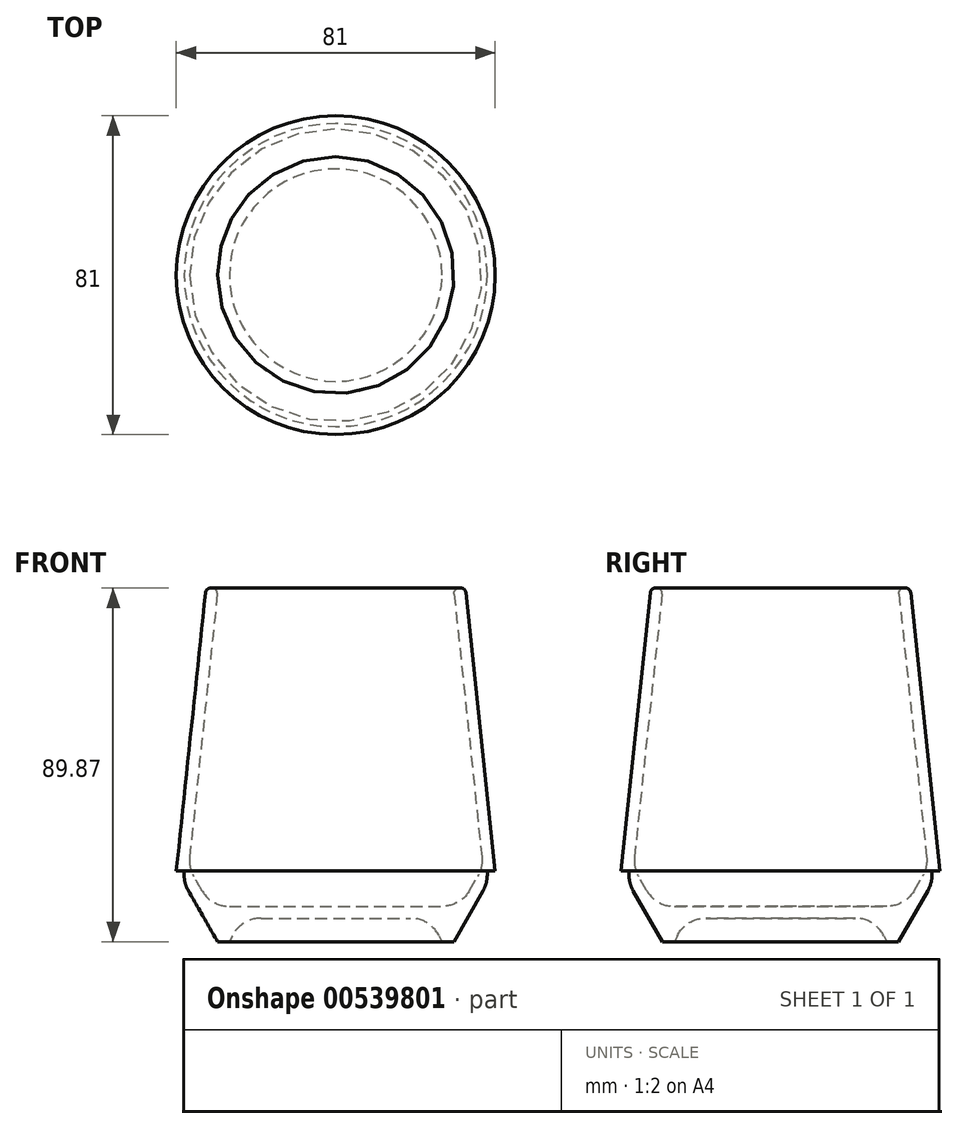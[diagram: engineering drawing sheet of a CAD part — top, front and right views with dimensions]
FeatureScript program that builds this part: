
annotation { "Feature Type Name" : "Feature", "Feature Type Description" : "" }
export const myFeature = defineFeature(function(context is Context, id is Id, definition is map)
    precondition{}
    {
        {
            var Q0;
            Q0=qCreatedBy(makeId("Front.planeOp"),FACE);
            var sketch = newSketch(context, id + "F0", { "sketchPlane" : qUnion([Q0])});
            skLineSegment(sketch, "E0", {"start": v(0, 6) * mm, "end": v(19, 6) * mm});
            skLineSegment(sketch, "E1", {"start": v(26.24, 1.52) * mm, "end": v(27, 0) * mm});
            skLineSegment(sketch, "E2", {"start": v(27, 0) * mm, "end": v(30, 0) * mm});
            skLineSegment(sketch, "E3", {"start": v(30, 0) * mm, "end": v(37.43, 12.97) * mm});
            skLineSegment(sketch, "E4", {"start": v(38.5, 17) * mm, "end": v(38.5, 18) * mm});
            skLineSegment(sketch, "E5", {"start": v(38.5, 18) * mm, "end": v(40.5, 18) * mm});
            skLineSegment(sketch, "E6", {"start": v(40.5, 18) * mm, "end": v(33.07, 88.7) * mm});
            skLineSegment(sketch, "E7", {"start": v(31.64, 89.86) * mm, "end": v(31.24, 89.82) * mm});
            skLineSegment(sketch, "E8", {"start": v(30.08, 88.4) * mm, "end": v(37.11, 21.54) * mm});
            skLineSegment(sketch, "E9", {"start": v(36.09, 16.67) * mm, "end": v(34.03, 13.08) * mm});
            skLineSegment(sketch, "E10", {"start": v(27, 9) * mm, "end": v(0, 9) * mm});
            skLineSegment(sketch, "E11", {"start": v(0, 9) * mm, "end": v(0, 6) * mm});
            skPoint(sketch, "E12.visualSharp", {"position": v(24, 6) * mm});
            skArc(sketch, "E12.filletArc", {"start": v(26.24, 1.52) * mm, "mid": v(23.25, 4.8) * mm, "end": v(19, 6) * mm});
            skPoint(sketch, "E13.visualSharp", {"position": v(31.7, 9) * mm});
            skArc(sketch, "E13.filletArc", {"start": v(27, 9) * mm, "mid": v(31.06, 10.1) * mm, "end": v(34.03, 13.08) * mm});
            skPoint(sketch, "E14.visualSharp", {"position": v(37.39, 18.94) * mm});
            skArc(sketch, "E14.filletArc", {"start": v(36.09, 16.67) * mm, "mid": v(36.98, 19.02) * mm, "end": v(37.11, 21.54) * mm});
            skPoint(sketch, "E15.visualSharp", {"position": v(38.5, 14.84) * mm});
            skArc(sketch, "E15.filletArc", {"start": v(37.43, 12.97) * mm, "mid": v(38.23, 14.92) * mm, "end": v(38.5, 17) * mm});
            skPoint(sketch, "E16.visualSharp", {"position": v(32.93, 90) * mm});
            skArc(sketch, "E16.filletArc", {"start": v(33.07, 88.7) * mm, "mid": v(32.6, 89.58) * mm, "end": v(31.64, 89.86) * mm});
            skPoint(sketch, "E17.visualSharp", {"position": v(29.95, 89.69) * mm});
            skArc(sketch, "E17.filletArc", {"start": v(31.24, 89.82) * mm, "mid": v(30.37, 89.35) * mm, "end": v(30.08, 88.4) * mm});
            skLineSegment(sketch, "E18", {"start": v(40.5, 18) * mm, "end": v(40.5, 90) * mm, "construction": true});
            skLineSegment(sketch, "E19", {"start": v(0, 0) * mm, "end": v(0, 88.7) * mm, "construction": true});
            skSolve(sketch);
        }
        {
            var Q0;
            Q0=qSketchRegion(id+"F0",true);
            var Q1;
            Q1=sQuery(id+"F0.wireOp",EDGE,"E19");
            revolve(context, id + "F1", {"entities" : qUnion([Q0]), "axis" : qUnion([Q1]), "revolveType" : RevolveType.FULL});
        }
    });
